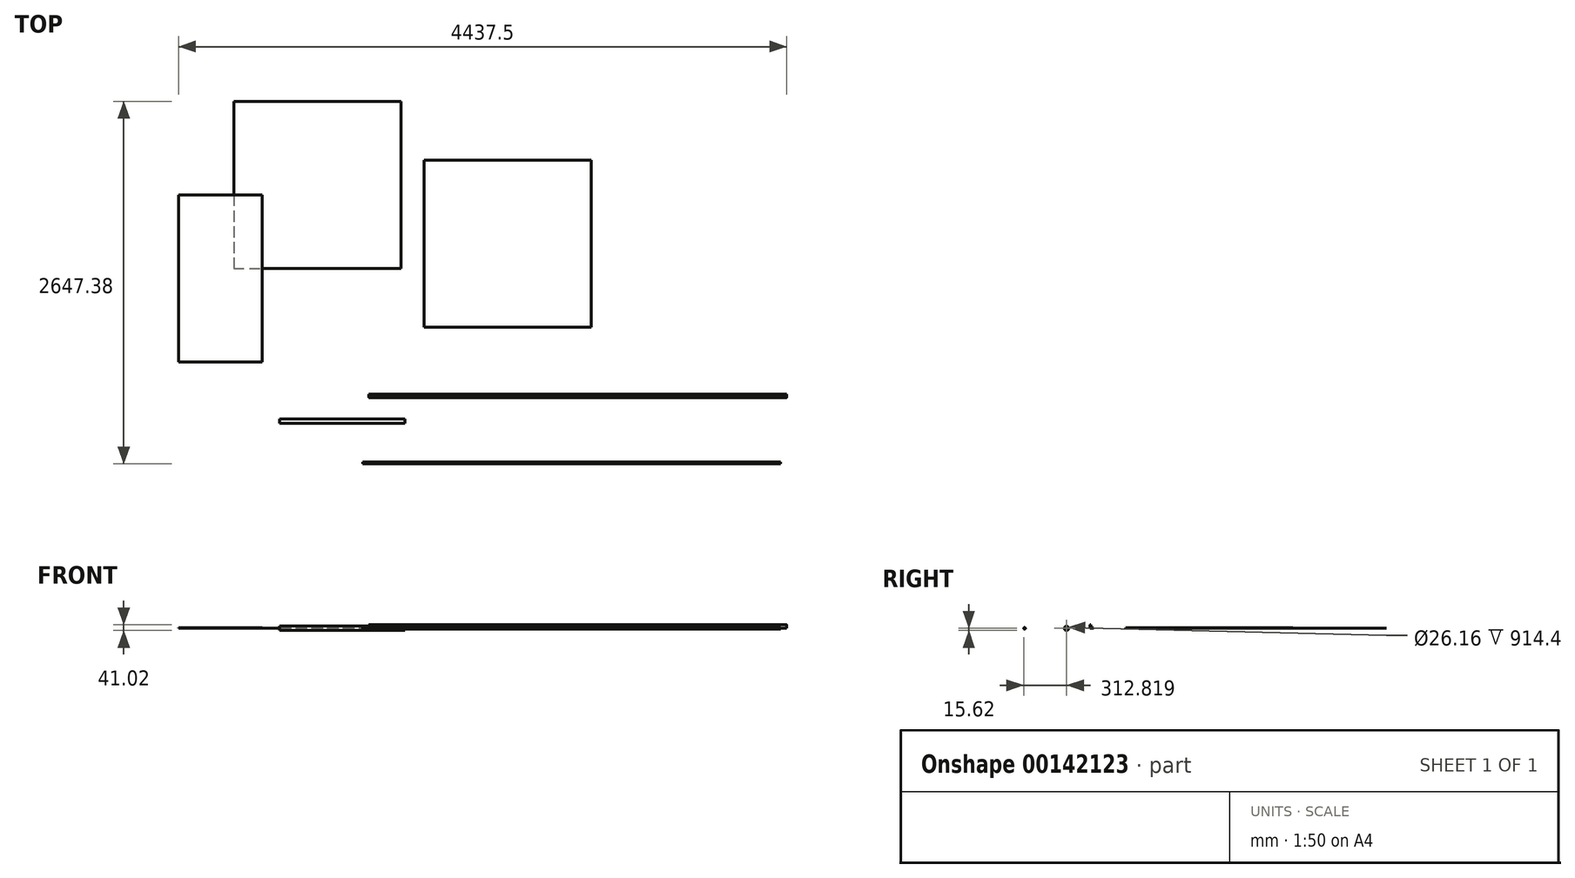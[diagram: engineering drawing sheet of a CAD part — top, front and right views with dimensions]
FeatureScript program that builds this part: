
annotation { "Feature Type Name" : "Feature", "Feature Type Description" : "" }
export const myFeature = defineFeature(function(context is Context, id is Id, definition is map)
    precondition{}
    {
        {
            var Q0;
            Q0=qCreatedBy(makeId("Top.planeOp"),FACE);
            var sketch = newSketch(context, id + "F0", { "sketchPlane" : qUnion([Q0])});
            skLineSegment(sketch, "E0.bottom", {"start": v(-1498.66, 1032.1) * mm, "end": v(-889.06, 1032.1) * mm});
            skLineSegment(sketch, "E0.top", {"start": v(-1498.66, -187.1) * mm, "end": v(-889.06, -187.1) * mm});
            skLineSegment(sketch, "E0.left", {"start": v(-1498.66, 1032.1) * mm, "end": v(-1498.66, -187.1) * mm});
            skLineSegment(sketch, "E0.right", {"start": v(-889.06, 1032.1) * mm, "end": v(-889.06, -187.1) * mm});
            skSolve(sketch);
        }
        {
            var Q0;
            Q0=qCreatedBy(makeId("Top.planeOp"),FACE);
            var sketch = newSketch(context, id + "F1", { "sketchPlane" : qUnion([Q0])});
            skLineSegment(sketch, "E1.bottom", {"start": v(-1095.22, 1714.72) * mm, "end": v(123.98, 1714.72) * mm});
            skLineSegment(sketch, "E1.top", {"start": v(-1095.22, 495.52) * mm, "end": v(123.98, 495.52) * mm});
            skLineSegment(sketch, "E1.left", {"start": v(-1095.22, 1714.72) * mm, "end": v(-1095.22, 495.52) * mm});
            skLineSegment(sketch, "E1.right", {"start": v(123.98, 1714.72) * mm, "end": v(123.98, 495.52) * mm});
            skSolve(sketch);
        }
        {
            var Q0;
            Q0=qCreatedBy(makeId("Top.planeOp"),FACE);
            var sketch = newSketch(context, id + "F2", { "sketchPlane" : qUnion([Q0])});
            skLineSegment(sketch, "E2.bottom", {"start": v(292.1, 1283.06) * mm, "end": v(1511.3, 1283.06) * mm});
            skLineSegment(sketch, "E2.top", {"start": v(292.1, 63.86) * mm, "end": v(1511.3, 63.86) * mm});
            skLineSegment(sketch, "E2.left", {"start": v(292.1, 1283.06) * mm, "end": v(292.1, 63.86) * mm});
            skLineSegment(sketch, "E2.right", {"start": v(1511.3, 1283.06) * mm, "end": v(1511.3, 63.86) * mm});
            skSolve(sketch);
        }
        {
            var Q0;
            Q0=qCreatedBy(makeId("Top.planeOp"),FACE);
            var sketch = newSketch(context, id + "F3", { "sketchPlane" : qUnion([Q0])});
            skLineSegment(sketch, "E3.bottom", {"start": v(-109.16, -423.15) * mm, "end": v(2938.84, -423.15) * mm});
            skLineSegment(sketch, "E3.top", {"start": v(-109.16, -448.55) * mm, "end": v(2938.84, -448.55) * mm});
            skLineSegment(sketch, "E3.left", {"start": v(-109.16, -423.15) * mm, "end": v(-109.16, -448.55) * mm});
            skLineSegment(sketch, "E3.right", {"start": v(2938.84, -423.15) * mm, "end": v(2938.84, -448.55) * mm});
            skSolve(sketch);
        }
        {
            var Q0;
            Q0=qCreatedBy(makeId("Top.planeOp"),FACE);
            var sketch = newSketch(context, id + "F4", { "sketchPlane" : qUnion([Q0])});
            skLineSegment(sketch, "E4.bottom", {"start": v(-759.94, -604.22) * mm, "end": v(154.46, -604.22) * mm});
            skLineSegment(sketch, "E4.top", {"start": v(-759.94, -619.84) * mm, "end": v(154.46, -619.84) * mm});
            skLineSegment(sketch, "E4.left", {"start": v(-759.94, -604.22) * mm, "end": v(-759.94, -619.84) * mm});
            skLineSegment(sketch, "E4.right", {"start": v(154.46, -604.22) * mm, "end": v(154.46, -619.84) * mm});
            skSolve(sketch);
        }
        {
            var Q0;
            Q0=qCreatedBy(makeId("Top.planeOp"),FACE);
            var sketch = newSketch(context, id + "F5", { "sketchPlane" : qUnion([Q0])});
            skLineSegment(sketch, "E5.bottom", {"start": v(-154.68, -919.96) * mm, "end": v(2893.32, -919.96) * mm});
            skLineSegment(sketch, "E5.top", {"start": v(-154.68, -926.31) * mm, "end": v(2893.32, -926.31) * mm});
            skLineSegment(sketch, "E5.left", {"start": v(-154.68, -919.96) * mm, "end": v(-154.68, -926.31) * mm});
            skLineSegment(sketch, "E5.right", {"start": v(2893.32, -919.96) * mm, "end": v(2893.32, -926.31) * mm});
            skSolve(sketch);
        }
        {
            var Q0;
            Q0 = qSketchRegion(id + "F0", true);
            extrude(context, id + "F6", {"entities" : qUnion([Q0]), "depth" : 3.04 * mm});
        }
        {
            var Q0;
            Q0 = qSketchRegion(id + "F1", true);
            extrude(context, id + "F7", {"entities" : qUnion([Q0]), "depth" : 1.9 * mm});
        }
        {
            var Q0;
            Q0 = qSketchRegion(id + "F2", true);
            extrude(context, id + "F8", {"entities" : qUnion([Q0]), "depth" : 1.9 * mm});
        }
        {
            var Q0;
            Q0 = qSketchRegion(id + "F3", true);
            extrude(context, id + "F9", {"entities" : qUnion([Q0]), "depth" : 25.4 * mm});
        }
        {
            var Q0;
            Q0 = qSketchRegion(id + "F4", true);
            var Q1;
            Q1=sQuery(id+"F4.wireOp",EDGE,"E4.top");
            revolve(context, id + "F10", {"entities" : qUnion([Q0]), "axis" : qUnion([Q1]), "revolveType" : RevolveType.FULL});
        }
        {
            var Q0;
            Q0=makeQuery(id+"F10.opRevolve","SWEPT_FACE",FACE,{"disambiguationData":[OSD([sQuery(id+"F4.wireOp",EDGE,"E4.left")])]});
            var sketch = newSketch(context, id + "F11", { "sketchPlane" : qUnion([Q0])});
            skCircle(sketch, "E6", {"center": v(619.84, 0) * mm, "radius": 13.08 * mm});
            skSolve(sketch);
        }
        {
            var Q0;
            Q0 = qSketchRegion(id + "F11", true);
            extrude(context, id + "F12", {"entities" : qUnion([Q0]), "operationType" : NewBodyOperationType.REMOVE, "endBound" : BoundingType.THROUGH_ALL, "oppositeDirection" : true, "depth" : 25.4 * mm});
        }
        {
            var Q0;
            Q0 = qSketchRegion(id + "F5", true);
            var Q1;
            Q1=sQuery(id+"F5.wireOp",EDGE,"E5.top");
            revolve(context, id + "F13", {"entities" : qUnion([Q0]), "axis" : qUnion([Q1]), "revolveType" : RevolveType.FULL});
        }
        {
            var Q0;
            Q0=makeQuery(id+"F9.opExtrude","SWEPT_FACE",FACE,{"disambiguationData":[OSD([sQuery(id+"F3.wireOp",EDGE,"E3.left")])]});
            var sketch = newSketch(context, id + "F14", { "sketchPlane" : qUnion([Q0])});
            skLineSegment(sketch, "E7.bottom", {"start": v(423.15, 25.4) * mm, "end": v(443.78, 25.4) * mm});
            skLineSegment(sketch, "E7.top", {"start": v(423.15, 4.76) * mm, "end": v(443.78, 4.76) * mm});
            skLineSegment(sketch, "E7.left", {"start": v(423.15, 25.4) * mm, "end": v(423.15, 4.76) * mm});
            skLineSegment(sketch, "E7.right", {"start": v(443.78, 25.4) * mm, "end": v(443.78, 4.76) * mm});
            skSolve(sketch);
        }
        {
            var Q0;
            Q0 = qSketchRegion(id + "F14", true);
            extrude(context, id + "F15", {"entities" : qUnion([Q0]), "operationType" : NewBodyOperationType.REMOVE, "endBound" : BoundingType.THROUGH_ALL, "oppositeDirection" : true, "depth" : 25.4 * mm});
        }
        {
            var Q0;
            Q0=makeQuery(id+"F15.boolean.opBoolean","COPY",EDGE,{"derivedFrom":makeQuery(id+"F15.opExtrude","SWEPT_EDGE",EDGE,{"disambiguationData":[OSD([sQuery(id+"F3.wireOp",EDGE,"E3.bottom"),sQuery(id+"F3.wireOp",EDGE,"E3.left"),sQuery(id+"F14.wireOp",EDGE,"E7.top"),sQuery(id+"F14.wireOp",EDGE,"E7.left")])]})});
            var Q1;
            Q1=makeQuery(id+"F15.boolean.opBoolean","COPY",EDGE,{"derivedFrom":makeQuery(id+"F15.opExtrude","SWEPT_EDGE",EDGE,{"disambiguationData":[OSD([sQuery(id+"F3.wireOp",EDGE,"E3.left"),sQuery(id+"F14.wireOp",EDGE,"E7.bottom"),sQuery(id+"F14.wireOp",EDGE,"E7.right")])]})});
            var Q2;
            Q2=makeQuery(id+"F9.opExtrude","CAP_EDGE",EDGE,{"disambiguationData":[OSD([sQuery(id+"F3.wireOp",EDGE,"E3.top")])],"isStart":false});
            var Q3;
            Q3=makeQuery(id+"F9.opExtrude","CAP_EDGE",EDGE,{"disambiguationData":[OSD([sQuery(id+"F3.wireOp",EDGE,"E3.bottom")])],"isStart":true});
            fillet(context, id + "F16", {"entities" : qUnion([Q0, Q1, Q2, Q3]), "radius" : 1.78 * mm, "tangentPropagation" : true, "allowEdgeOverflow" : false});
        }
    });
